# Revit family: Filtered_Supply_Centrifugal-Carnes-VNBL
name_source: partatom
category: Mechanical Equipment
revit_build: Autodesk Revit MEP 2012 (Build: 20110309_2315(x64)
units: mm (PartAtom-declared; Revit-internal decimal feet)

## types (5) — shared parameters
04 CSI = 23 37 13
95 CSI = 15850
Amperage = 0 A
Apparent Load = 0 VA
Assembly Code = D3040200
Catalog URL = http://www.carnes.com
Default Elevation = 0"
Description = Filtered Supply Centrifugal
E = 1 7/8"
Frequency = 0 Hz
IOM Instructions URL = http://www.carnes.com
Manufacturer = CARNES COMPANY
Manufacturer Fax = 608-845-6470
Model = VNBL
Number of Poles = 1
Phase = 1
Product Page URL = http://www.carnes.com
Spec Sheet URL = http://www.carnes.com
Subcategory = Filtered Supply Centrifugal
URL = http://www.carnes.com
Unit = Metal - Carnes - Steel
Voltage = 0 V
Wattage = 0 W
ecoScorecard Product Page = http://ecoscorecard.com
zero-valued in all types: Power Factor

## per-type parameters (varying)
| type | A | B sq. | C | D | F | G | H | I | J |
| 10 @ 45° | 24 1/2" | 29 3/4" | 21 3/4" | 21 1/8" | 8 7/8" | 9 1/4" | 13 7/8" | 11 5/8" | 23 3/4" |
| 12 @ 45° | 31 1/2" | 33 3/4" | 29" | 28 1/8" | 9 1/8" | 10 1/8" | 15 3/4" | 13 5/8" | 27 3/4" |
| 15 @ 45° | 31 1/2" | 33 3/4" | 29" | 28 1/8" | 7 5/8" | 9 7/8" | 18 7/8" | 16 1/8" | 27 3/4" |
| 18 @ 45° | 35 1/2" | 39 3/4" | 32 1/8" | 32 1/8" | 9" | 13 1/4" | 22 1/8" | 19 1/8" | 33 3/4" |
| 20 @ 45° | 47 1/2" | 45 3/4" | 40 1/8" | 44 1/8" | 11 1/2" | 14 1/2" | 23" | 25" | 39 3/4" |

## geometry (parser evidence)
native form markers: Blend x2, Sweep x6
no freeform markers — native parametric forms only
